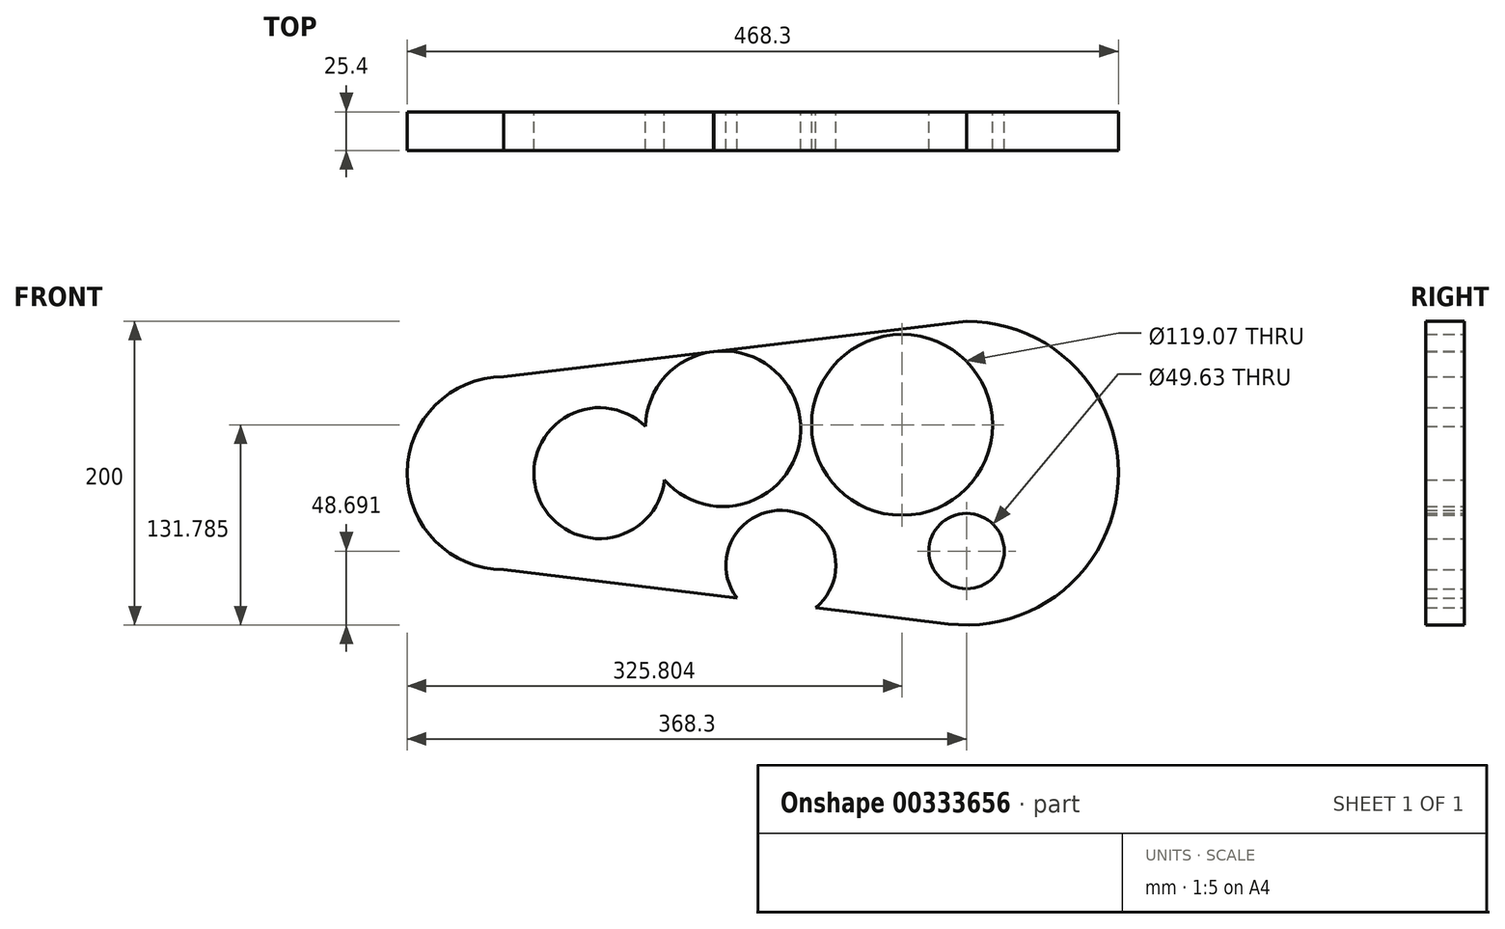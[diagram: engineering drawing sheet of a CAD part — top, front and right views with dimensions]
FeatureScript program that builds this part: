
annotation { "Feature Type Name" : "Feature", "Feature Type Description" : "" }
export const myFeature = defineFeature(function(context is Context, id is Id, definition is map)
    precondition{}
    {
        {
            var Q0;
            Q0=qCreatedBy(makeId("Front.planeOp"),FACE);
            var sketch = newSketch(context, id + "F0", { "sketchPlane" : qUnion([Q0])});
            skArc(sketch, "E0", {"start": v(-12.13, -99.26) * mm, "mid": v(99.82, -6.08) * mm, "end": v(0, 100) * mm});
            skArc(sketch, "E1", {"start": v(-304.8, 63.5) * mm, "mid": v(-368.3, 0) * mm, "end": v(-304.8, -63.5) * mm});
            skLineSegment(sketch, "E2", {"start": v(-304.8, 63.5) * mm, "end": v(0, 100) * mm});
            skLineSegment(sketch, "E3", {"start": v(-304.8, -63.5) * mm, "end": v(-12.13, -99.26) * mm});
            skPoint(sketch, "E4.orphan", {"position": v(0, -100.74) * mm});
            skCircle(sketch, "E5", {"center": v(-241.75, 0) * mm, "radius": 43.1 * mm});
            skCircle(sketch, "E6", {"center": v(-160.35, 29.24) * mm, "radius": 51.2 * mm});
            skCircle(sketch, "E7", {"center": v(-42.5, 31.78) * mm, "radius": 59.53 * mm});
            skCircle(sketch, "E8", {"center": v(-122.2, -60.64) * mm, "radius": 36.15 * mm});
            skCircle(sketch, "E9", {"center": v(0, -51.3) * mm, "radius": 24.81 * mm});
            skSolve(sketch);
        }
        {
            var Q0;
            {var subQ0=sQuery(id+"F0.wireOp",EDGE,"E6");var subQ1=sQuery(id+"F0.wireOp",EDGE,"E2");var subQ2=makeQuery(id+"F0.imprint","INTERSECT",VERTEX,{"disambiguationData":[OD(0.0)],"derivedFrom":[subQ1,subQ0]});Q0=makeQuery(id+"F0.imprint","IMPRINT",FACE,{"disambiguationData":[TD([[makeQuery(id+"F0.imprint","IMPRINT",EDGE,{"disambiguationData":[TD([[subQ2,-1.0]])],"derivedFrom":subQ1}),1.0]])]});}
            var Q1;
            {var subQ0=sQuery(id+"F0.wireOp",EDGE,"E8");var subQ1=sQuery(id+"F0.wireOp",EDGE,"E3");var subQ2=makeQuery(id+"F0.imprint","INTERSECT",VERTEX,{"disambiguationData":[OD(0.0)],"derivedFrom":[subQ1,subQ0]});Q1=makeQuery(id+"F0.imprint","IMPRINT",FACE,{"disambiguationData":[TD([[makeQuery(id+"F0.imprint","IMPRINT",EDGE,{"disambiguationData":[TD([[subQ2,-1.0]])],"derivedFrom":subQ1}),-1.0]])]});}
            var Q2;
            {var subQ0=sQuery(id+"F0.wireOp",EDGE,"E8");var subQ1=sQuery(id+"F0.wireOp",EDGE,"E3");var subQ2=makeQuery(id+"F0.imprint","INTERSECT",VERTEX,{"disambiguationData":[OD(0.0)],"derivedFrom":[subQ1,subQ0]});Q2=makeQuery(id+"F0.imprint","IMPRINT",FACE,{"disambiguationData":[TD([[makeQuery(id+"F0.imprint","IMPRINT",EDGE,{"disambiguationData":[TD([[subQ2,-1.0]])],"derivedFrom":subQ1}),1.0]])]});}
            var Q3;
            {var subQ5=sQuery(id+"F0.wireOp",EDGE,"E0");Q3=makeQuery(id+"F0.imprint","IMPRINT",FACE,{"disambiguationData":[TD([[makeQuery(id+"F0.imprint","IMPRINT",EDGE,{"derivedFrom":subQ5}),1.0]])]});}
            extrude(context, id + "F1", {"entities" : qUnion([Q0, Q1, Q2, Q3]), "depth" : 25.4 * mm});
        }
    });
